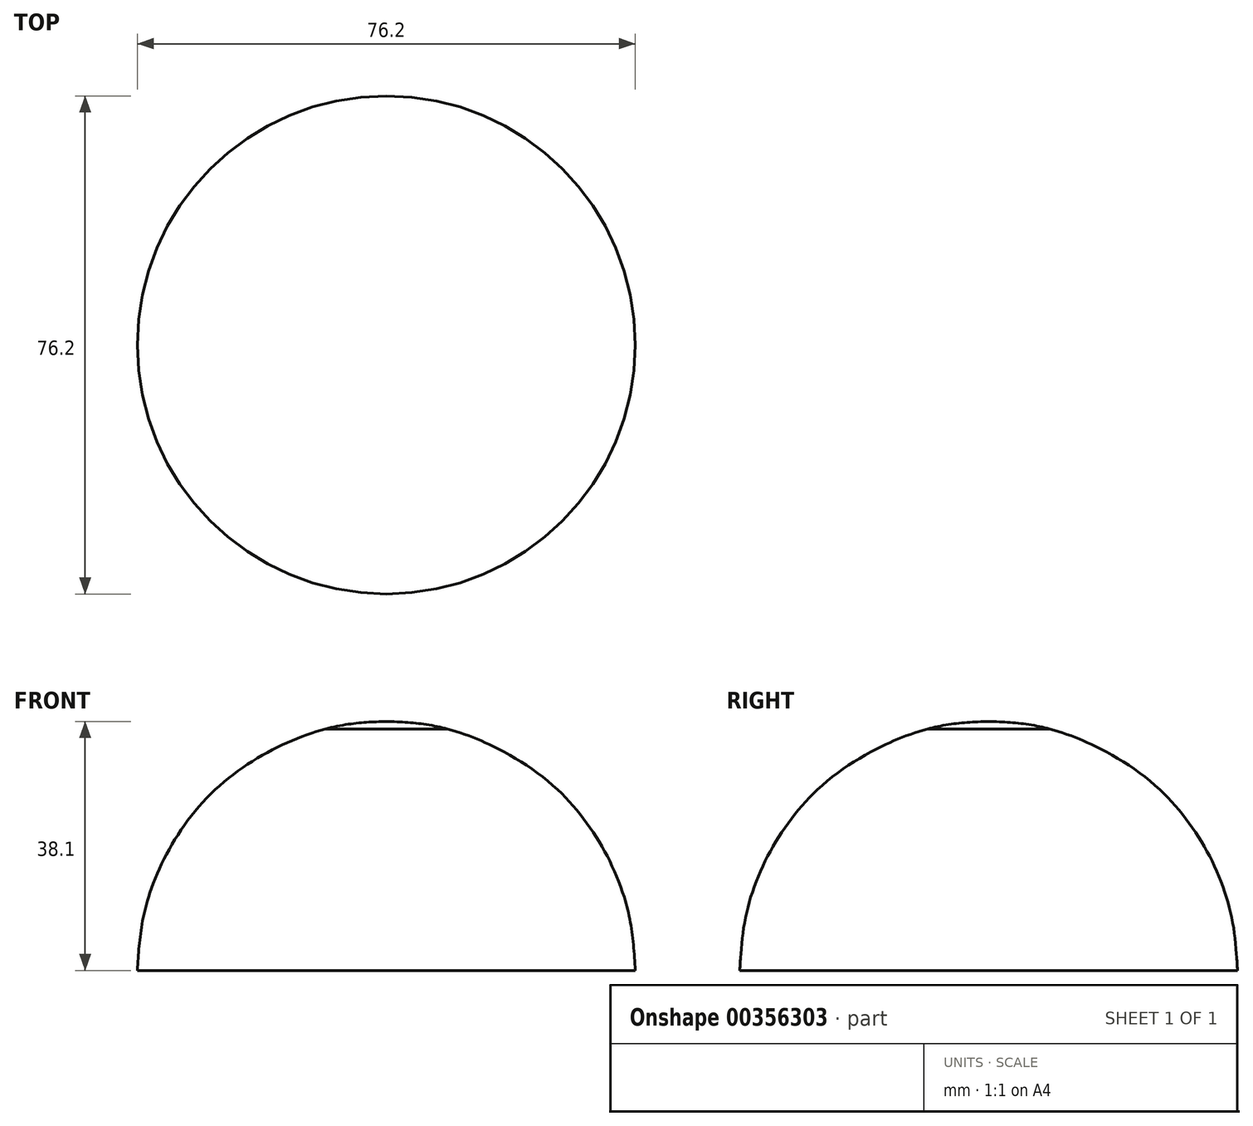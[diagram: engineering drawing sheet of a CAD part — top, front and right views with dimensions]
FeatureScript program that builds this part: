
annotation { "Feature Type Name" : "Feature", "Feature Type Description" : "" }
export const myFeature = defineFeature(function(context is Context, id is Id, definition is map)
    precondition{}
    {
        {
            var Q0;
            Q0=qCreatedBy(makeId("Front.planeOp"),FACE);
            var sketch = newSketch(context, id + "F0", { "sketchPlane" : qUnion([Q0])});
            skLineSegment(sketch, "E0", {"start": v(0, 0) * mm, "end": v(-38.1, 0) * mm});
            skLineSegment(sketch, "E1", {"start": v(0, 0) * mm, "end": v(0, 38.1) * mm});
            skLineSegment(sketch, "E2", {"start": v(0, 0) * mm, "end": v(-26.21, 27.65) * mm});
            skLineSegment(sketch, "E3", {"start": v(0, 0) * mm, "end": v(-36.42, 11.2) * mm});
            skLineSegment(sketch, "E4", {"start": v(0, 0) * mm, "end": v(-9.36, 36.93) * mm});
            skFitSpline(sketch, "E5", {"points": [v(0, 38.1) * mm, v(-9.36, 36.93) * mm, v(-26.21, 27.65) * mm, v(-36.42, 11.2) * mm, v(-38.1, 0) * mm], "startDerivative": vector(-42.78, -1.47) * mm, "endDerivative": vector(-2.8, -48.1) * mm});
            skSolve(sketch);
        }
        {
            var Q0;
            Q0=qSketchRegion(id+"F0",true);
            var Q1;
            Q1=sQuery(id+"F0.wireOp",EDGE,"E1");
            revolve(context, id + "F1", {"entities" : qUnion([Q0]), "axis" : qUnion([Q1]), "revolveType" : RevolveType.FULL});
        }
    });
